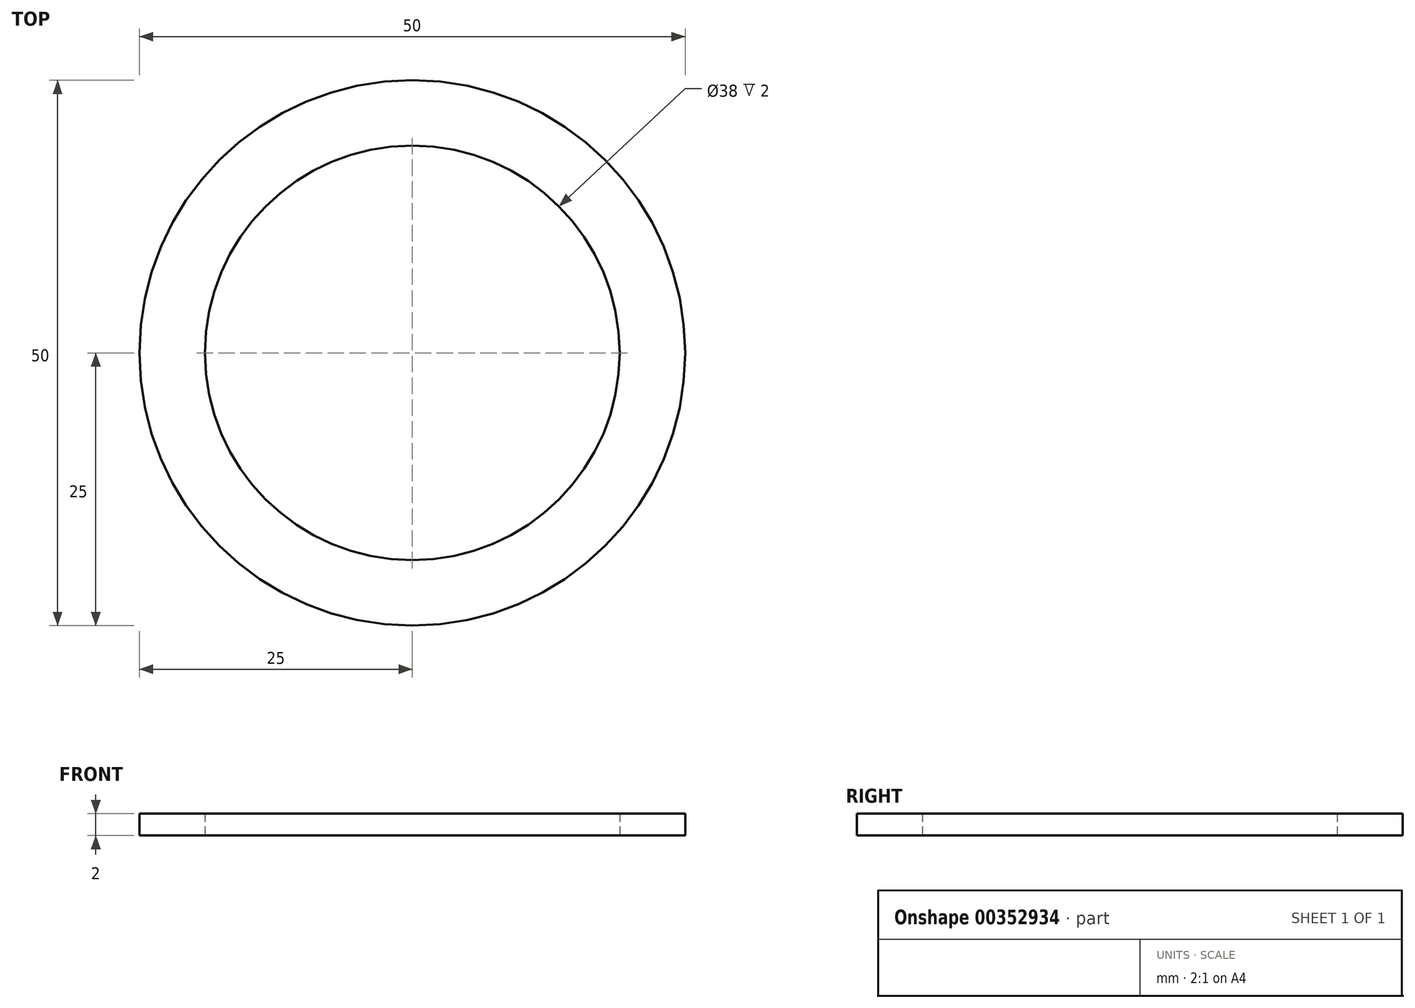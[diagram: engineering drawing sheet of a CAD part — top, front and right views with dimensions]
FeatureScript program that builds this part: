
annotation { "Feature Type Name" : "Feature", "Feature Type Description" : "" }
export const myFeature = defineFeature(function(context is Context, id is Id, definition is map)
    precondition{}
    {
        {
            var Q0;
            Q0=qCreatedBy(makeId("Top.planeOp"),FACE);
            var sketch = newSketch(context, id + "F0", { "sketchPlane" : qUnion([Q0])});
            skCircle(sketch, "E0", {"center": v(0, 0) * mm, "radius": 25 * mm});
            skCircle(sketch, "E1", {"center": v(0, 0) * mm, "radius": 19 * mm});
            skSolve(sketch);
        }
        {
            var Q0;
            Q0=makeQuery(id+"F0.imprint","IMPRINT",FACE,{"disambiguationData":[TD([[makeQuery(id+"F0.imprint","IMPRINT",EDGE,{"derivedFrom":sQuery(id+"F0.wireOp",EDGE,"E0")}),1.0]])]});
            extrude(context, id + "F1", {"entities" : qUnion([Q0]), "depth" : 2 * mm});
        }
    });
